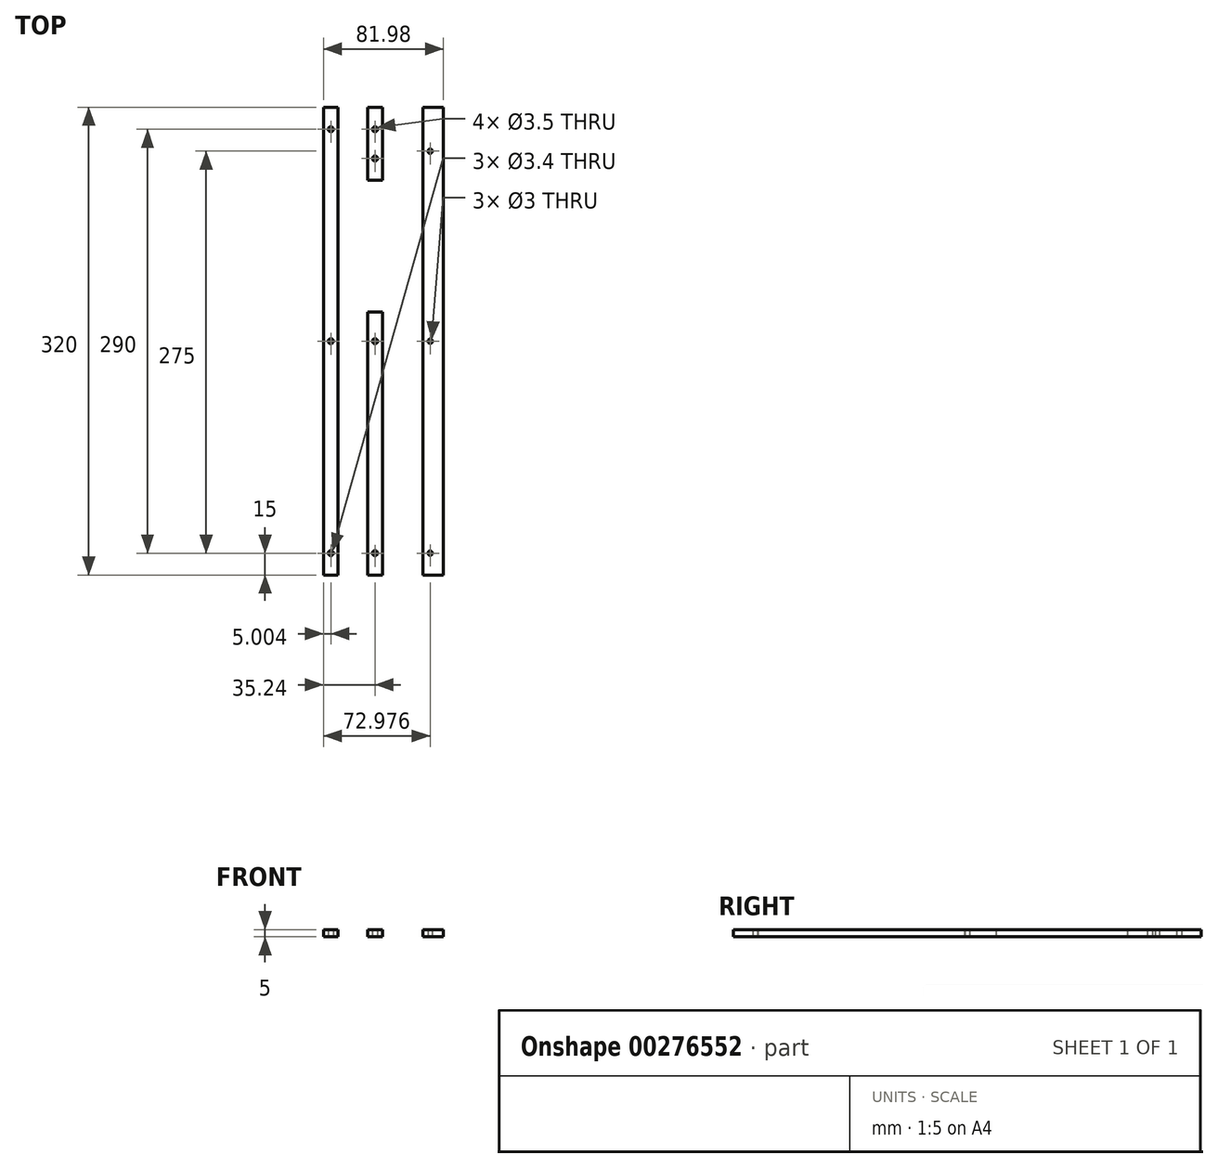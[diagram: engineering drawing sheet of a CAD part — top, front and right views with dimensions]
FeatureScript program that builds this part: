
annotation { "Feature Type Name" : "Feature", "Feature Type Description" : "" }
export const myFeature = defineFeature(function(context is Context, id is Id, definition is map)
    precondition{}
    {
        {
            var Q0;
            Q0=qCreatedBy(makeId("Top.planeOp"),FACE);
            var sketch = newSketch(context, id + "F0", { "sketchPlane" : qUnion([Q0])});
            skLineSegment(sketch, "E0.bottom", {"start": v(5, -160) * mm, "end": v(-5, -160) * mm});
            skLineSegment(sketch, "E0.top", {"start": v(5, 160) * mm, "end": v(-5, 160) * mm});
            skLineSegment(sketch, "E0.left", {"start": v(5, -160) * mm, "end": v(5, 160) * mm});
            skLineSegment(sketch, "E0.right", {"start": v(-5, -160) * mm, "end": v(-5, 160) * mm});
            skPoint(sketch, "E0.middle", {"position": v(0, 0) * mm});
            skSolve(sketch);
        }
        {
            var Q0;
            Q0 = qSketchRegion(id + "F0", true);
            extrude(context, id + "F1", {"entities" : qUnion([Q0]), "depth" : 5 * mm});
        }
        {
            var Q0;
            Q0=makeQuery(id+"F1.opExtrude","CAP_FACE",FACE,{"disambiguationData":[OSD([sQuery(id+"F0.wireOp",EDGE,"E0.bottom"),sQuery(id+"F0.wireOp",EDGE,"E0.top"),sQuery(id+"F0.wireOp",EDGE,"E0.left"),sQuery(id+"F0.wireOp",EDGE,"E0.right")])],"isStart":false});
            var sketch = newSketch(context, id + "F2", { "sketchPlane" : qUnion([Q0])});
            skPoint(sketch, "E1", {"position": v(0, -145) * mm});
            skPoint(sketch, "E2", {"position": v(0, 0) * mm});
            skPoint(sketch, "E3", {"position": v(0, 145) * mm});
            skPoint(sketch, "E4", {"position": v(0, 125) * mm});
            skSolve(sketch);
        }
        {
            var Q0;
            Q0=sQuery(id+"F2.wireOp",VERTEX,"E3");
            var Q1;
            Q1=sQuery(id+"F2.wireOp",VERTEX,"E2");
            var Q2;
            Q2=sQuery(id+"F2.wireOp",VERTEX,"E1");
            var Q3;
            Q3=sQuery(id+"F2.wireOp",VERTEX,"E4");
            var Q4;
            Q4=makeQuery(id+"F1.opExtrude","SWEPT_BODY",BODY,{"disambiguationData":[OSD([sQuery(id+"F0.wireOp",EDGE,"E0.bottom"),sQuery(id+"F0.wireOp",EDGE,"E0.top"),sQuery(id+"F0.wireOp",EDGE,"E0.left"),sQuery(id+"F0.wireOp",EDGE,"E0.right")])]});
            hole(context, id + "F3", {"style" : HoleStyle.SIMPLE, "endStyle" : HoleEndStyle.THROUGH, "holeDiameter" : 3.5 * mm, "tappedDepth" : 12 * mm, "tapClearance" : 3, "locations" : qUnion([Q0, Q1, Q2, Q3]), "scope" : qUnion([Q4])});
        }
        {
            var Q0;
            Q0=qCreatedBy(makeId("Top.planeOp"),FACE);
            var sketch = newSketch(context, id + "F4", { "sketchPlane" : qUnion([Q0])});
            skLineSegment(sketch, "E5.bottom", {"start": v(46.74, 160) * mm, "end": v(32.74, 160) * mm});
            skLineSegment(sketch, "E5.top", {"start": v(46.74, -160) * mm, "end": v(32.74, -160) * mm});
            skLineSegment(sketch, "E5.left", {"start": v(46.74, 160) * mm, "end": v(46.74, -160) * mm});
            skLineSegment(sketch, "E5.right", {"start": v(32.74, 160) * mm, "end": v(32.74, -160) * mm});
            skPoint(sketch, "E5.middle", {"position": v(39.74, 0) * mm});
            skSolve(sketch);
        }
        {
            var Q0;
            Q0 = qSketchRegion(id + "F4", true);
            extrude(context, id + "F5", {"entities" : qUnion([Q0]), "depth" : 5 * mm});
        }
        {
            var Q0;
            Q0=makeQuery(id+"F5.opExtrude","CAP_FACE",FACE,{"disambiguationData":[OSD([sQuery(id+"F4.wireOp",EDGE,"E5.bottom"),sQuery(id+"F4.wireOp",EDGE,"E5.top"),sQuery(id+"F4.wireOp",EDGE,"E5.left"),sQuery(id+"F4.wireOp",EDGE,"E5.right")])],"isStart":false});
            var sketch = newSketch(context, id + "F6", { "sketchPlane" : qUnion([Q0])});
            skPoint(sketch, "E6", {"position": v(37.74, -145) * mm});
            skPoint(sketch, "E7", {"position": v(37.74, 0) * mm});
            skPoint(sketch, "E7.positionSnap0", {"position": v(46.74, 0) * mm});
            skPoint(sketch, "E8", {"position": v(37.74, 130) * mm});
            skSolve(sketch);
        }
        {
            var Q0;
            Q0=sQuery(id+"F6.wireOp",VERTEX,"E8");
            var Q1;
            Q1=sQuery(id+"F6.wireOp",VERTEX,"E7");
            var Q2;
            Q2=sQuery(id+"F6.wireOp",VERTEX,"E6");
            var Q3;
            Q3=makeQuery(id+"F5.opExtrude","SWEPT_BODY",BODY,{"disambiguationData":[OSD([sQuery(id+"F4.wireOp",EDGE,"E5.bottom"),sQuery(id+"F4.wireOp",EDGE,"E5.top"),sQuery(id+"F4.wireOp",EDGE,"E5.left"),sQuery(id+"F4.wireOp",EDGE,"E5.right")])]});
            hole(context, id + "F7", {"style" : HoleStyle.SIMPLE, "endStyle" : HoleEndStyle.THROUGH, "holeDiameter" : 3 * mm, "tappedDepth" : 12 * mm, "tapClearance" : 3, "locations" : qUnion([Q0, Q1, Q2]), "scope" : qUnion([Q3])});
        }
        {
            var Q0;
            Q0=makeQuery(id+"F1.opExtrude","CAP_FACE",FACE,{"disambiguationData":[OSD([sQuery(id+"F0.wireOp",EDGE,"E0.bottom"),sQuery(id+"F0.wireOp",EDGE,"E0.top"),sQuery(id+"F0.wireOp",EDGE,"E0.left"),sQuery(id+"F0.wireOp",EDGE,"E0.right")])],"isStart":false});
            var sketch = newSketch(context, id + "F8", { "sketchPlane" : qUnion([Q0])});
            skLineSegment(sketch, "E9.bottom", {"start": v(-5, 20) * mm, "end": v(5, 20) * mm});
            skLineSegment(sketch, "E9.top", {"start": v(-5, 110) * mm, "end": v(5, 110) * mm});
            skLineSegment(sketch, "E9.left", {"start": v(-5, 20) * mm, "end": v(-5, 110) * mm});
            skLineSegment(sketch, "E9.right", {"start": v(5, 20) * mm, "end": v(5, 110) * mm});
            skSolve(sketch);
        }
        {
            var Q0;
            Q0 = qSketchRegion(id + "F8", true);
            extrude(context, id + "F9", {"entities" : qUnion([Q0]), "operationType" : NewBodyOperationType.REMOVE, "oppositeDirection" : true, "depth" : 25 * mm});
        }
        {
            var Q0;
            Q0=qCreatedBy(makeId("Top.planeOp"),FACE);
            var sketch = newSketch(context, id + "F10", { "sketchPlane" : qUnion([Q0])});
            skLineSegment(sketch, "E10.bottom", {"start": v(-35.24, 160) * mm, "end": v(-25.24, 160) * mm});
            skLineSegment(sketch, "E10.top", {"start": v(-35.24, -160) * mm, "end": v(-25.24, -160) * mm});
            skLineSegment(sketch, "E10.left", {"start": v(-35.24, 160) * mm, "end": v(-35.24, -160) * mm});
            skLineSegment(sketch, "E10.right", {"start": v(-25.24, 160) * mm, "end": v(-25.24, -160) * mm});
            skPoint(sketch, "E10.middle", {"position": v(-30.24, 0) * mm});
            skSolve(sketch);
        }
        {
            var Q0;
            Q0 = qSketchRegion(id + "F10", true);
            extrude(context, id + "F11", {"entities" : qUnion([Q0]), "depth" : 5 * mm});
        }
        {
            var Q0;
            Q0=makeQuery(id+"F11.opExtrude","CAP_FACE",FACE,{"disambiguationData":[OSD([sQuery(id+"F10.wireOp",EDGE,"E10.bottom"),sQuery(id+"F10.wireOp",EDGE,"E10.top"),sQuery(id+"F10.wireOp",EDGE,"E10.left"),sQuery(id+"F10.wireOp",EDGE,"E10.right")])],"isStart":false});
            var sketch = newSketch(context, id + "F12", { "sketchPlane" : qUnion([Q0])});
            skPoint(sketch, "E11", {"position": v(-30.24, -145) * mm});
            skPoint(sketch, "E12", {"position": v(-30.24, 0) * mm});
            skPoint(sketch, "E13", {"position": v(-30.24, 145) * mm});
            skSolve(sketch);
        }
        {
            var Q0;
            Q0=sQuery(id+"F12.wireOp",VERTEX,"E13");
            var Q1;
            Q1=sQuery(id+"F12.wireOp",VERTEX,"E12");
            var Q2;
            Q2=sQuery(id+"F12.wireOp",VERTEX,"E11");
            var Q3;
            Q3=makeQuery(id+"F11.opExtrude","SWEPT_BODY",BODY,{"disambiguationData":[OSD([sQuery(id+"F10.wireOp",EDGE,"E10.bottom"),sQuery(id+"F10.wireOp",EDGE,"E10.top"),sQuery(id+"F10.wireOp",EDGE,"E10.left"),sQuery(id+"F10.wireOp",EDGE,"E10.right")])]});
            hole(context, id + "F13", {"style" : HoleStyle.SIMPLE, "endStyle" : HoleEndStyle.THROUGH, "holeDiameter" : 3.4 * mm, "tappedDepth" : 12 * mm, "tapClearance" : 3, "locations" : qUnion([Q0, Q1, Q2]), "scope" : qUnion([Q3])});
        }
    });
